# Revit family: RS201.80.x.150
name_source: partatom
category: Sanitärinstallationen
units: mm (PartAtom-declared; Revit-internal decimal feet)

## family parameters
Arbeitsebenenbasiert = Nein
Beim Laden mit Abzugskörper schneiden = Nein
Bemaßung runder Anschluss = Durchmesser verwenden
Gemeinsam genutzt = Nein
Immer vertikal = Ja
Raumberechnungspunkt = Nein
Teiletyp = Normal

## types (2) — shared parameters
Baugruppenkennzeichen = D2030300
Hersteller = Resitec
RS_AVol-H = 200 mm  [stored 0.656168 ft]
RS_AVol-L = 129 mm  [stored 0.423228 ft]
RS_AVol-T = 129 mm  [stored 0.423228 ft]
RS_DVol-L = 200 mm  [stored 0.656168 ft]
RS_DVol-T = 200 mm  [stored 0.656168 ft]
RS_Klbl = 2 mm  [stored 0.00656168 ft]
RS_Manufacture = Resitec
RS_URL = https://resitec.ch
RS_dia001 = 150 mm
RS_dia002 = 130 mm  [stored 0.426509 ft]
RS_dim001 = 16 mm  [stored 0.0524934 ft]
RS_dim003 = 22 mm
RS_s = 1 mm  [stored 0.00328084 ft]
RS_s001 = 3 mm  [stored 0.00984252 ft]
URL = https://www.resitec.ch
zero-valued in all types: Anschlusswert DU L/s, Vorgabe-Ansicht

## per-type parameters (varying)
| type | RS_DN1 | RS_DN1d | RS_DN2 | RS_dim002 |
| DN60 | 60 mm  [stored 0.19685 ft] | 76 mm  [stored 0.249344 ft] | 63 mm  [stored 0.206693 ft] | 24 mm  [stored 0.0787402 ft] |
| DN80 | 80 mm  [stored 0.262467 ft] | 89 mm | 76 mm  [stored 0.249344 ft] | 23 mm  [stored 0.0754593 ft] |

note: [stored X ft] marks values corroborated as IEEE doubles in the binary element streams (Revit-internal decimal feet)

## geometry (parser evidence)
native form markers: Blend x8
no freeform markers — native parametric forms only
